# Revit family: ALMA-Zander_Roll_Mat
name_source: partatom
category: Specialty Equipment
units: mm (PartAtom-declared; Revit-internal decimal feet)

## family parameters
Always vertical = Yes
Cut with Voids When Loaded = No
Enable Cutting in Views = Yes
Maintain Annotation Orientation = No
Part Type = Normal
Room Calculation Point = No
Round Connector Dimension = Use Diameter
Shared = No
Work Plane-Based = No

## types (3) — shared parameters
Grip_Material = BM_MATTE BLACK
Length = 450 mm  [stored 1.47638 ft]
Thickness = 10 mm  [stored 0.0328084 ft]
Width = 400 mm  [stored 1.31234 ft]
zero-valued in all types: Default Elevation

## per-type parameters (varying)
| type | RollMat_Material |
| STAINLESS STEEL (KACR001) | BM_STAINLESS STEEL |
| BRASS GOLD (KAGD002) | BM_BRASS GOLD |
| GUNMETAL (KAGM004) | BM_GUNMETAL |

note: [stored X ft] marks values corroborated as IEEE doubles in the binary element streams (Revit-internal decimal feet)

## geometry (parser evidence)
native form markers: Sweep x2
no freeform markers — native parametric forms only
